# Revit family: 305_4b54c4118bb54e789e42f1291e4ff8
name_source: partatom
category: Pipe Accessories
revit_build: Autodesk Revit 2018 (Build: 20170223_1515(x64)
units: mm (PartAtom-declared; Revit-internal decimal feet)

## family parameters
Always vertical = Yes
Cut with Voids When Loaded = No
Part Type = Valve - Breaks Into
Round Connector Dimension = Use Diameter
Shared = No
Work Plane-Based = No

## types (3) — shared parameters
CAT0 = Yes
Description = Giacoqest Valve
HD1 = 4 mm  [stored 0.0131234 ft]
L2D_Min = 3048 mm
Manufacturer = Giacomini
QmdConnectorList = 301;D;302;D
URL = http://www.giacomini.com
magiPartTypeId = 305
magiProductFamilyId = 4b54c4118bb54e789e42f1291e4ff8
zero-valued in all types: MC_Default_elevation

## per-type parameters (varying)
- GZ651Y003: C=63 mm  [stored 0.206693 ft]; CenSd_H2_6=11 mm; D=15 mm; H2=13 mm  [stored 0.0426509 ft]; H4=9 mm  [stored 0.0295276 ft]; HD2=13 mm  [stored 0.0426509 ft]; HD21=13 mm  [stored 0.0426509 ft]; I=30 mm  [stored 0.0984252 ft]; J=16 mm  [stored 0.0524934 ft]; J3=13 mm  [stored 0.0426509 ft]; L2=30 mm  [stored 0.0984252 ft]; L2D=60 mm; L3=11 mm; L3__ve=-11 mm; L4=7 mm  [stored 0.0229659 ft]; L4__ve=-7 mm; L5=12 mm  [stored 0.0393701 ft]; L6=3 mm  [stored 0.00984252 ft]; L6__ve=-3 mm  [stored -0.00984252 ft]; L7=9 mm  [stored 0.0295276 ft]; LL=28 mm; LL__ve=-28 mm; R1=8 mm  [stored 0.0262467 ft]; R2=9 mm  [stored 0.0295276 ft]; S1=25 mm  [stored 0.082021 ft]; S1__ve=-25 mm; W2D=15 mm  [stored 0.0492126 ft]; magiProductId=2b9c62c915d145269959bab3da0bcd
- GZ651Y005: C=73 mm; CenSd_H2_6=18 mm; D=25 mm; H2=21 mm; H4=14 mm  [stored 0.0459318 ft]; HD2=15 mm  [stored 0.0492126 ft]; HD21=15 mm  [stored 0.0492126 ft]; I=41 mm; J=25 mm  [stored 0.082021 ft]; J3=21 mm; L2=41 mm; L2D=81 mm; L3=15 mm  [stored 0.0492126 ft]; L3__ve=-15 mm  [stored -0.0492126 ft]; L4=10 mm  [stored 0.0328084 ft]; L4__ve=-10 mm  [stored -0.0328084 ft]; L5=16 mm  [stored 0.0524934 ft]; L6=4 mm  [stored 0.0131234 ft]; L6__ve=-4 mm  [stored -0.0131234 ft]; L7=12 mm  [stored 0.0393701 ft]; LL=38 mm  [stored 0.124672 ft]; LL__ve=-38 mm; R1=12 mm  [stored 0.0393701 ft]; R2=15 mm  [stored 0.0492126 ft]; S1=32 mm  [stored 0.104987 ft]; S1__ve=-32 mm; W2D=25 mm  [stored 0.082021 ft]; magiProductId=3a34642973ba4e94b0cf8f83de4568
- GZ651Y004: C=73 mm; CenSd_H2_6=14 mm  [stored 0.0459318 ft]; D=20 mm; H2=16 mm  [stored 0.0524934 ft]; H4=11 mm; HD2=15 mm  [stored 0.0492126 ft]; HD21=15 mm  [stored 0.0492126 ft]; I=34 mm; J=21 mm; J3=17 mm; L2=34 mm; L2D=68 mm; L3=12 mm  [stored 0.0393701 ft]; L3__ve=-12 mm  [stored -0.0393701 ft]; L4=8 mm  [stored 0.0262467 ft]; L4__ve=-8 mm  [stored -0.0262467 ft]; L5=14 mm  [stored 0.0459318 ft]; L6=3 mm  [stored 0.00984252 ft]; L6__ve=-3 mm  [stored -0.00984252 ft]; L7=10 mm  [stored 0.0328084 ft]; LL=32 mm  [stored 0.104987 ft]; LL__ve=-32 mm; R1=10 mm  [stored 0.0328084 ft]; R2=12 mm  [stored 0.0393701 ft]; S1=28 mm; S1__ve=-28 mm; W2D=20 mm  [stored 0.0656168 ft]; magiProductId=168c186aa02f435b9cdb7ddfa04b47

note: column(s) folded — value = type name in every type: magiProductCode

note: [stored X ft] marks values corroborated as IEEE doubles in the binary element streams (Revit-internal decimal feet)

## geometry (parser evidence)
native form markers: Sweep x1
no freeform markers — native parametric forms only
